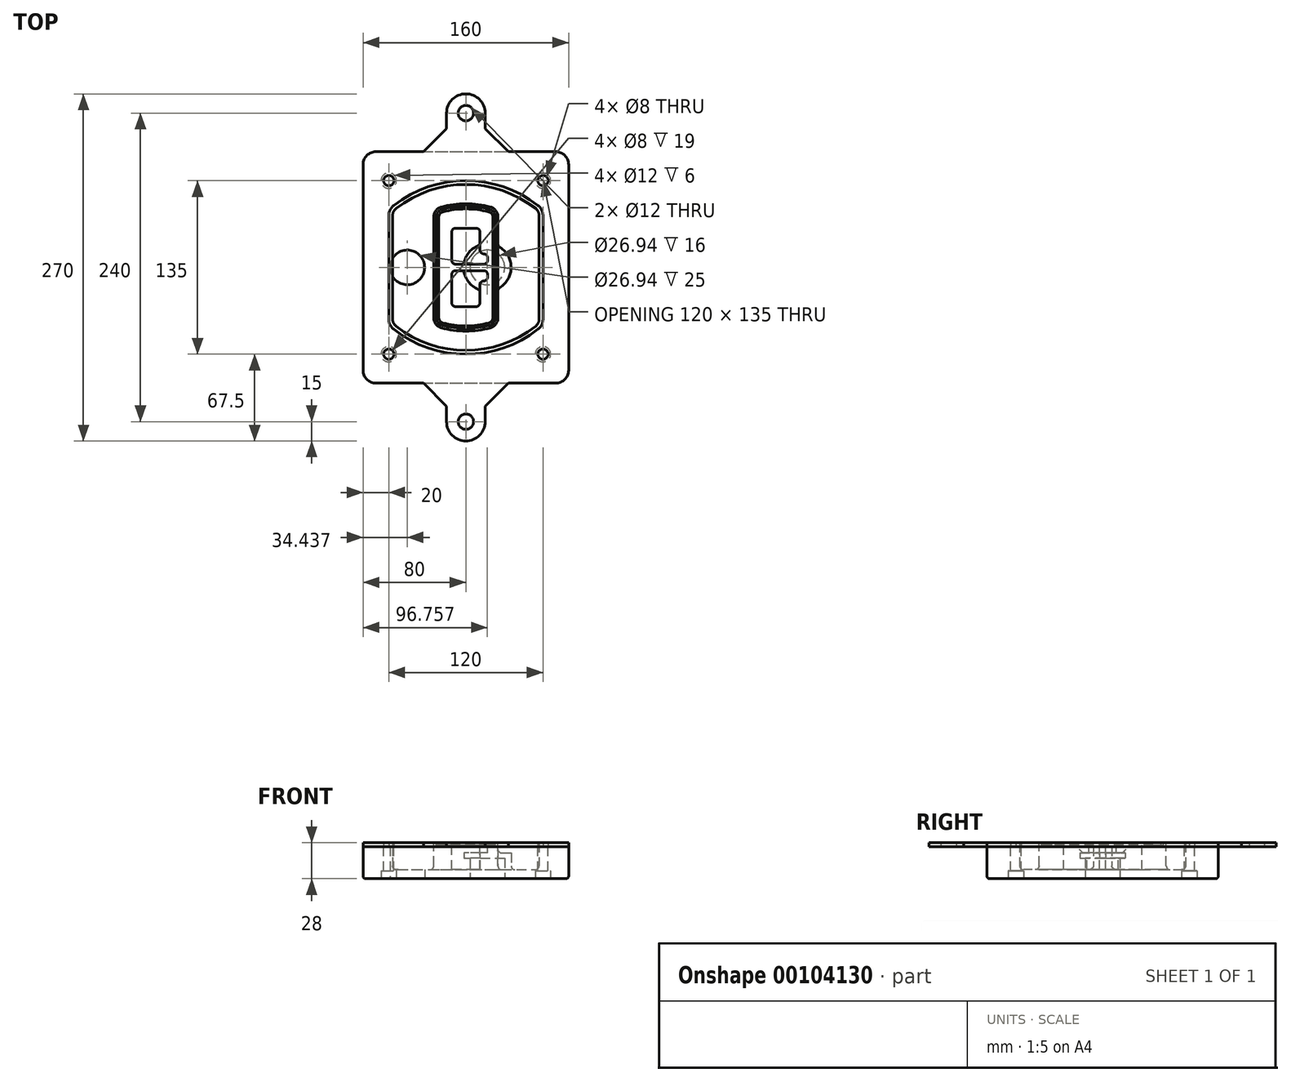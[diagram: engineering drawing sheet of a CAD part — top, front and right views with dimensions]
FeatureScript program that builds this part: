
annotation { "Feature Type Name" : "Feature", "Feature Type Description" : "" }
export const myFeature = defineFeature(function(context is Context, id is Id, definition is map)
    precondition{}
    {
        {
            var Q0;
            Q0=qCreatedBy(makeId("Top.planeOp"),FACE);
            var sketch = newSketch(context, id + "F0", { "sketchPlane" : qUnion([Q0])});
            skPoint(sketch, "E0.rect.middle", {"position": v(0, 0) * mm});
            skLineSegment(sketch, "E1.bottom", {"start": v(-70, -90) * mm, "end": v(70, -90) * mm});
            skLineSegment(sketch, "E1.top", {"start": v(-70, 90) * mm, "end": v(70, 90) * mm});
            skLineSegment(sketch, "E1.left", {"start": v(-80, -80) * mm, "end": v(-80, 80) * mm});
            skLineSegment(sketch, "E1.right", {"start": v(80, -80) * mm, "end": v(80, 80) * mm});
            skLineSegment(sketch, "E2", {"start": v(-80, 90) * mm, "end": v(80, -90) * mm, "construction": true});
            skLineSegment(sketch, "E3", {"start": v(80, 90) * mm, "end": v(-80, -90) * mm, "construction": true});
            skCircle(sketch, "E4", {"center": v(-60, 67.5) * mm, "radius": 4 * mm});
            skCircle(sketch, "E5", {"center": v(60, 67.5) * mm, "radius": 4 * mm});
            skCircle(sketch, "E6", {"center": v(60, -67.5) * mm, "radius": 4 * mm});
            skCircle(sketch, "E7", {"center": v(-60, -67.5) * mm, "radius": 4 * mm});
            skLineSegment(sketch, "E8", {"start": v(-60, 67.5) * mm, "end": v(60, 67.5) * mm, "construction": true});
            skLineSegment(sketch, "E9", {"start": v(60, 67.5) * mm, "end": v(60, -67.5) * mm, "construction": true});
            skLineSegment(sketch, "E10", {"start": v(60, -67.5) * mm, "end": v(-60, -67.5) * mm, "construction": true});
            skLineSegment(sketch, "E11", {"start": v(-60, -67.5) * mm, "end": v(-60, 67.5) * mm, "construction": true});
            skLineSegment(sketch, "E12", {"start": v(-60, 40.3) * mm, "end": v(-60, -40.3) * mm});
            skLineSegment(sketch, "E13", {"start": v(60, 40.3) * mm, "end": v(60, -40.3) * mm});
            skArc(sketch, "E14", {"start": v(56.15, 48.18) * mm, "mid": v(0, 67.5) * mm, "end": v(-56.15, 48.18) * mm});
            skArc(sketch, "E15", {"start": v(-56.15, -48.18) * mm, "mid": v(0, -67.5) * mm, "end": v(56.15, -48.18) * mm});
            skLineSegment(sketch, "E16", {"start": v(-60, 0) * mm, "end": v(60, 0) * mm, "construction": true});
            skPoint(sketch, "E17.visualSharp", {"position": v(-60, -45) * mm});
            skArc(sketch, "E17.filletArc", {"start": v(-60, -40.3) * mm, "mid": v(-58.99, -44.68) * mm, "end": v(-56.15, -48.18) * mm});
            skPoint(sketch, "E18.visualSharp", {"position": v(-60, 45) * mm});
            skArc(sketch, "E18.filletArc", {"start": v(-56.15, 48.18) * mm, "mid": v(-58.99, 44.68) * mm, "end": v(-60, 40.3) * mm});
            skPoint(sketch, "E19.visualSharp", {"position": v(60, 45) * mm});
            skArc(sketch, "E19.filletArc", {"start": v(60, 40.3) * mm, "mid": v(58.99, 44.68) * mm, "end": v(56.15, 48.18) * mm});
            skPoint(sketch, "E20.visualSharp", {"position": v(60, -45) * mm});
            skArc(sketch, "E20.filletArc", {"start": v(56.15, -48.18) * mm, "mid": v(58.99, -44.68) * mm, "end": v(60, -40.3) * mm});
            skPoint(sketch, "E21.visualSharp", {"position": v(-80, 90) * mm});
            skArc(sketch, "E21.filletArc", {"start": v(-70, 90) * mm, "mid": v(-77.07, 87.07) * mm, "end": v(-80, 80) * mm});
            skPoint(sketch, "E22.visualSharp", {"position": v(80, 90) * mm});
            skArc(sketch, "E22.filletArc", {"start": v(80, 80) * mm, "mid": v(77.07, 87.07) * mm, "end": v(70, 90) * mm});
            skPoint(sketch, "E23.visualSharp", {"position": v(80, -90) * mm});
            skArc(sketch, "E23.filletArc", {"start": v(70, -90) * mm, "mid": v(77.07, -87.07) * mm, "end": v(80, -80) * mm});
            skPoint(sketch, "E24.visualSharp", {"position": v(-80, -90) * mm});
            skArc(sketch, "E24.filletArc", {"start": v(-80, -80) * mm, "mid": v(-77.07, -87.07) * mm, "end": v(-70, -90) * mm});
            skArc(sketch, "E25.0", {"start": v(57, 40.3) * mm, "mid": v(56.3, 43.36) * mm, "end": v(54.3, 45.81) * mm});
            skLineSegment(sketch, "E25.1", {"start": v(57, 40.3) * mm, "end": v(57, -40.3) * mm});
            skArc(sketch, "E25.2", {"start": v(54.3, -45.81) * mm, "mid": v(56.3, -43.36) * mm, "end": v(57, -40.3) * mm});
            skArc(sketch, "E25.3", {"start": v(-54.3, -45.81) * mm, "mid": v(0, -64.5) * mm, "end": v(54.3, -45.81) * mm});
            skArc(sketch, "E25.4", {"start": v(-57, -40.3) * mm, "mid": v(-56.3, -43.36) * mm, "end": v(-54.3, -45.81) * mm});
            skArc(sketch, "E25.5", {"start": v(54.3, 45.81) * mm, "mid": v(0, 64.5) * mm, "end": v(-54.3, 45.81) * mm});
            skLineSegment(sketch, "E25.6", {"start": v(-57, 40.3) * mm, "end": v(-57, -40.3) * mm});
            skArc(sketch, "E25.7", {"start": v(-54.3, 45.81) * mm, "mid": v(-56.3, 43.36) * mm, "end": v(-57, 40.3) * mm});
            skArc(sketch, "E26.0", {"start": v(-58.62, 51.33) * mm, "mid": v(-62.58, 46.43) * mm, "end": v(-64, 40.3) * mm});
            skArc(sketch, "E26.1", {"start": v(58.62, 51.33) * mm, "mid": v(0, 71.5) * mm, "end": v(-58.62, 51.33) * mm});
            skArc(sketch, "E26.2", {"start": v(64, 40.3) * mm, "mid": v(62.58, 46.43) * mm, "end": v(58.62, 51.33) * mm});
            skLineSegment(sketch, "E26.3", {"start": v(64, 40.3) * mm, "end": v(64, -40.3) * mm});
            skArc(sketch, "E26.4", {"start": v(58.62, -51.33) * mm, "mid": v(62.58, -46.43) * mm, "end": v(64, -40.3) * mm});
            skLineSegment(sketch, "E26.5", {"start": v(-64, 40.3) * mm, "end": v(-64, -40.3) * mm});
            skArc(sketch, "E26.6", {"start": v(-58.62, -51.33) * mm, "mid": v(0, -71.5) * mm, "end": v(58.62, -51.33) * mm});
            skArc(sketch, "E26.7", {"start": v(-64, -40.3) * mm, "mid": v(-62.58, -46.43) * mm, "end": v(-58.62, -51.33) * mm});
            skSolve(sketch);
        }
        {
            var Q0;
            Q0=makeQuery(id+"F0.imprint","IMPRINT",FACE,{"disambiguationData":[TD([[makeQuery(id+"F0.imprint","IMPRINT",EDGE,{"derivedFrom":sQuery(id+"F0.wireOp",EDGE,"E1.bottom")}),1.0]])]});
            var Q1;
            Q1=makeQuery(id+"F0.imprint","IMPRINT",FACE,{"disambiguationData":[TD([[makeQuery(id+"F0.imprint","IMPRINT",EDGE,{"derivedFrom":sQuery(id+"F0.wireOp",EDGE,"E12")}),1.0]])]});
            var Q2;
            Q2=makeQuery(id+"F0.imprint","IMPRINT",FACE,{"disambiguationData":[TD([[makeQuery(id+"F0.imprint","IMPRINT",EDGE,{"derivedFrom":sQuery(id+"F0.wireOp",EDGE,"E25.0")}),1.0]])]});
            var Q3;
            Q3=makeQuery(id+"F0.imprint","IMPRINT",FACE,{"disambiguationData":[TD([[makeQuery(id+"F0.imprint","IMPRINT",EDGE,{"derivedFrom":sQuery(id+"F0.wireOp",EDGE,"E12")}),-1.0]])]});
            extrude(context, id + "F1", {"entities" : qUnion([Q0, Q1, Q2, Q3]), "oppositeDirection" : true, "depth" : 25 * mm});
        }
        {
            var Q0;
            Q0=makeQuery(id+"F0.imprint","IMPRINT",FACE,{"disambiguationData":[TD([[makeQuery(id+"F0.imprint","IMPRINT",EDGE,{"derivedFrom":sQuery(id+"F0.wireOp",EDGE,"E12")}),1.0]])]});
            extrude(context, id + "F2", {"entities" : qUnion([Q0]), "operationType" : NewBodyOperationType.ADD, "depth" : 3 * mm});
        }
        {
            var Q0;
            Q0=makeQuery(id+"F0.imprint","IMPRINT",FACE,{"disambiguationData":[TD([[makeQuery(id+"F0.imprint","IMPRINT",EDGE,{"derivedFrom":sQuery(id+"F0.wireOp",EDGE,"E25.0")}),1.0]])]});
            extrude(context, id + "F3", {"entities" : qUnion([Q0]), "operationType" : NewBodyOperationType.REMOVE, "oppositeDirection" : true, "depth" : 18 * mm});
        }
        {
            var Q0;
            Q0=makeQuery(id+"F2.opExtrude","CAP_FACE",FACE,{"disambiguationData":[OSD([sQuery(id+"F0.wireOp",EDGE,"E12"),sQuery(id+"F0.wireOp",EDGE,"E13"),sQuery(id+"F0.wireOp",EDGE,"E14"),sQuery(id+"F0.wireOp",EDGE,"E15"),sQuery(id+"F0.wireOp",EDGE,"E17.filletArc"),sQuery(id+"F0.wireOp",EDGE,"E18.filletArc"),sQuery(id+"F0.wireOp",EDGE,"E19.filletArc"),sQuery(id+"F0.wireOp",EDGE,"E20.filletArc"),sQuery(id+"F0.wireOp",EDGE,"E25.0"),sQuery(id+"F0.wireOp",EDGE,"E25.1"),sQuery(id+"F0.wireOp",EDGE,"E25.2"),sQuery(id+"F0.wireOp",EDGE,"E25.3"),sQuery(id+"F0.wireOp",EDGE,"E25.4"),sQuery(id+"F0.wireOp",EDGE,"E25.5"),sQuery(id+"F0.wireOp",EDGE,"E25.6"),sQuery(id+"F0.wireOp",EDGE,"E25.7")])],"isStart":false});
            var sketch = newSketch(context, id + "F4", { "sketchPlane" : qUnion([Q0])});
            skArc(sketch, "E27.0", {"start": v(-19.08, -46.97) * mm, "mid": v(0, -49.5) * mm, "end": v(19.08, -46.97) * mm});
            skArc(sketch, "E28.0", {"start": v(19.08, 46.97) * mm, "mid": v(0, 49.5) * mm, "end": v(-19.08, 46.97) * mm});
            skLineSegment(sketch, "E29", {"start": v(-25, 39.25) * mm, "end": v(-25, -39.25) * mm});
            skLineSegment(sketch, "E30", {"start": v(25, 39.25) * mm, "end": v(25, -39.25) * mm});
            skLineSegment(sketch, "E31", {"start": v(-25, 45.1) * mm, "end": v(25, 45.1) * mm, "construction": true});
            skLineSegment(sketch, "E32", {"start": v(-25, -45.1) * mm, "end": v(25, -45.1) * mm, "construction": true});
            skPoint(sketch, "E33.visualSharp", {"position": v(-25, 45.1) * mm});
            skArc(sketch, "E33.filletArc", {"start": v(-19.08, 46.97) * mm, "mid": v(-23.35, 44.11) * mm, "end": v(-25, 39.25) * mm});
            skPoint(sketch, "E34.visualSharp", {"position": v(25, 45.1) * mm});
            skArc(sketch, "E34.filletArc", {"start": v(25, 39.25) * mm, "mid": v(23.35, 44.11) * mm, "end": v(19.08, 46.97) * mm});
            skPoint(sketch, "E35.visualSharp", {"position": v(25, -45.1) * mm});
            skArc(sketch, "E35.filletArc", {"start": v(19.08, -46.97) * mm, "mid": v(23.35, -44.11) * mm, "end": v(25, -39.25) * mm});
            skPoint(sketch, "E36.visualSharp", {"position": v(-25, -45.1) * mm});
            skArc(sketch, "E36.filletArc", {"start": v(-25, -39.25) * mm, "mid": v(-23.35, -44.11) * mm, "end": v(-19.08, -46.97) * mm});
            skArc(sketch, "E37.0", {"start": v(54.3, 45.81) * mm, "mid": v(0, 64.5) * mm, "end": v(-54.3, 45.81) * mm});
            skArc(sketch, "E37.1", {"start": v(-54.3, 45.81) * mm, "mid": v(-56.3, 43.36) * mm, "end": v(-57, 40.3) * mm});
            skLineSegment(sketch, "E37.2", {"start": v(-57, 40.3) * mm, "end": v(-57, -40.3) * mm});
            skArc(sketch, "E37.3", {"start": v(-57, -40.3) * mm, "mid": v(-56.3, -43.36) * mm, "end": v(-54.3, -45.81) * mm});
            skArc(sketch, "E37.4", {"start": v(-54.3, -45.81) * mm, "mid": v(0, -64.5) * mm, "end": v(54.3, -45.81) * mm});
            skArc(sketch, "E37.5", {"start": v(54.3, -45.81) * mm, "mid": v(56.3, -43.36) * mm, "end": v(57, -40.3) * mm});
            skLineSegment(sketch, "E37.6", {"start": v(57, 40.3) * mm, "end": v(57, -40.3) * mm});
            skArc(sketch, "E37.7", {"start": v(57, 40.3) * mm, "mid": v(56.3, 43.36) * mm, "end": v(54.3, 45.81) * mm});
            skLineSegment(sketch, "E38.0", {"start": v(23, 39.25) * mm, "end": v(23, -39.25) * mm});
            skArc(sketch, "E38.1", {"start": v(18.56, -45.04) * mm, "mid": v(21.76, -42.9) * mm, "end": v(23, -39.25) * mm});
            skArc(sketch, "E38.2", {"start": v(-18.56, -45.04) * mm, "mid": v(0, -47.5) * mm, "end": v(18.56, -45.04) * mm});
            skArc(sketch, "E38.3", {"start": v(-23, -39.25) * mm, "mid": v(-21.76, -42.9) * mm, "end": v(-18.56, -45.04) * mm});
            skLineSegment(sketch, "E38.4", {"start": v(-23, 39.25) * mm, "end": v(-23, -39.25) * mm});
            skArc(sketch, "E38.5", {"start": v(23, 39.25) * mm, "mid": v(21.76, 42.9) * mm, "end": v(18.56, 45.04) * mm});
            skArc(sketch, "E38.6", {"start": v(-18.56, 45.04) * mm, "mid": v(-21.76, 42.9) * mm, "end": v(-23, 39.25) * mm});
            skArc(sketch, "E38.7", {"start": v(18.56, 45.04) * mm, "mid": v(0, 47.5) * mm, "end": v(-18.56, 45.04) * mm});
            skArc(sketch, "E39.0", {"start": v(21, 39.25) * mm, "mid": v(20.18, 41.68) * mm, "end": v(18.04, 43.1) * mm});
            skLineSegment(sketch, "E39.1", {"start": v(21, 39.25) * mm, "end": v(21, -39.25) * mm});
            skArc(sketch, "E39.2", {"start": v(18.04, -43.1) * mm, "mid": v(20.18, -41.68) * mm, "end": v(21, -39.25) * mm});
            skArc(sketch, "E39.3", {"start": v(-18.04, -43.1) * mm, "mid": v(0, -45.5) * mm, "end": v(18.04, -43.1) * mm});
            skArc(sketch, "E39.4", {"start": v(-21, -39.25) * mm, "mid": v(-20.18, -41.68) * mm, "end": v(-18.04, -43.1) * mm});
            skArc(sketch, "E39.5", {"start": v(18.04, 43.1) * mm, "mid": v(0, 45.5) * mm, "end": v(-18.04, 43.1) * mm});
            skLineSegment(sketch, "E39.6", {"start": v(-21, 39.25) * mm, "end": v(-21, -39.25) * mm});
            skArc(sketch, "E39.7", {"start": v(-18.04, 43.1) * mm, "mid": v(-20.18, 41.68) * mm, "end": v(-21, 39.25) * mm});
            skLineSegment(sketch, "E40", {"start": v(-25, 0) * mm, "end": v(25, 0) * mm, "construction": true});
            skLineSegment(sketch, "E41", {"start": v(-11, 5.5) * mm, "end": v(-11, 27.5) * mm});
            skLineSegment(sketch, "E42", {"start": v(-8, 30.5) * mm, "end": v(8, 30.5) * mm});
            skLineSegment(sketch, "E43", {"start": v(11, 27.5) * mm, "end": v(11, 13.5) * mm});
            skLineSegment(sketch, "E44", {"start": v(14, 10.5) * mm, "end": v(14, 10.5) * mm});
            skLineSegment(sketch, "E45", {"start": v(17, 7.5) * mm, "end": v(17, 5.5) * mm});
            skLineSegment(sketch, "E46", {"start": v(14, 2.5) * mm, "end": v(-8, 2.5) * mm});
            skPoint(sketch, "E47.visualSharp", {"position": v(-11, 30.5) * mm});
            skArc(sketch, "E47.filletArc", {"start": v(-8, 30.5) * mm, "mid": v(-10.12, 29.62) * mm, "end": v(-11, 27.5) * mm});
            skPoint(sketch, "E48.visualSharp", {"position": v(11, 30.5) * mm});
            skArc(sketch, "E48.filletArc", {"start": v(11, 27.5) * mm, "mid": v(10.12, 29.62) * mm, "end": v(8, 30.5) * mm});
            skPoint(sketch, "E49.visualSharp", {"position": v(11, 10.5) * mm});
            skArc(sketch, "E49.filletArc", {"start": v(11, 13.5) * mm, "mid": v(11.88, 11.38) * mm, "end": v(14, 10.5) * mm});
            skPoint(sketch, "E50.visualSharp", {"position": v(17, 10.5) * mm});
            skArc(sketch, "E50.filletArc", {"start": v(17, 7.5) * mm, "mid": v(16.12, 9.62) * mm, "end": v(14, 10.5) * mm});
            skPoint(sketch, "E51.visualSharp", {"position": v(17, 2.5) * mm});
            skArc(sketch, "E51.filletArc", {"start": v(14, 2.5) * mm, "mid": v(16.12, 3.38) * mm, "end": v(17, 5.5) * mm});
            skPoint(sketch, "E52.visualSharp", {"position": v(-11, 2.5) * mm});
            skArc(sketch, "E52.filletArc", {"start": v(-11, 5.5) * mm, "mid": v(-10.12, 3.38) * mm, "end": v(-8, 2.5) * mm});
            skLineSegment(sketch, "E53.0.MirrorCS", {"start": v(14, -2.5) * mm, "end": v(-8, -2.5) * mm});
            skArc(sketch, "E54.0.MirrorCS", {"start": v(-11, -5.5) * mm, "mid": v(-10.12, -3.38) * mm, "end": v(-8, -2.5) * mm});
            skLineSegment(sketch, "E55.0.MirrorCS", {"start": v(-11, -5.5) * mm, "end": v(-11, -27.5) * mm});
            skArc(sketch, "E56.0.MirrorCS", {"start": v(-8, -30.5) * mm, "mid": v(-10.12, -29.62) * mm, "end": v(-11, -27.5) * mm});
            skLineSegment(sketch, "E57.0.MirrorCS", {"start": v(-8, -30.5) * mm, "end": v(8, -30.5) * mm});
            skArc(sketch, "E58.0.MirrorCS", {"start": v(11, -27.5) * mm, "mid": v(10.12, -29.62) * mm, "end": v(8, -30.5) * mm});
            skLineSegment(sketch, "E59.0.MirrorCS", {"start": v(11, -27.5) * mm, "end": v(11, -13.5) * mm});
            skArc(sketch, "E60.0.MirrorCS", {"start": v(11, -13.5) * mm, "mid": v(11.88, -11.38) * mm, "end": v(14, -10.5) * mm});
            skArc(sketch, "E61.0.MirrorCS", {"start": v(17, -7.5) * mm, "mid": v(16.12, -9.62) * mm, "end": v(14, -10.5) * mm});
            skLineSegment(sketch, "E62.0.MirrorCS", {"start": v(17, -7.5) * mm, "end": v(17, -5.5) * mm});
            skArc(sketch, "E63.0.MirrorCS", {"start": v(14, -2.5) * mm, "mid": v(16.12, -3.38) * mm, "end": v(17, -5.5) * mm});
            skSolve(sketch);
        }
        {
            var Q0;
            Q0=makeQuery(id+"F4.imprint","IMPRINT",FACE,{"disambiguationData":[TD([[makeQuery(id+"F4.imprint","IMPRINT",EDGE,{"derivedFrom":sQuery(id+"F4.wireOp",EDGE,"E27.0")}),1.0]])]});
            var Q1;
            Q1=makeQuery(id+"F4.imprint","IMPRINT",FACE,{"disambiguationData":[TD([[makeQuery(id+"F4.imprint","IMPRINT",EDGE,{"derivedFrom":sQuery(id+"F4.wireOp",EDGE,"E38.0")}),-1.0]])]});
            var Q2;
            Q2=makeQuery(id+"F4.imprint","IMPRINT",FACE,{"disambiguationData":[TD([[makeQuery(id+"F4.imprint","IMPRINT",EDGE,{"derivedFrom":sQuery(id+"F4.wireOp",EDGE,"E39.0")}),1.0]])]});
            extrude(context, id + "F5", {"entities" : qUnion([Q0, Q1, Q2]), "operationType" : NewBodyOperationType.ADD, "endBound" : BoundingType.UP_TO_NEXT, "oppositeDirection" : true, "depth" : 25 * mm});
        }
        {
            var Q0;
            Q0=makeQuery(id+"F4.imprint","IMPRINT",FACE,{"disambiguationData":[TD([[makeQuery(id+"F4.imprint","IMPRINT",EDGE,{"derivedFrom":sQuery(id+"F4.wireOp",EDGE,"E38.0")}),-1.0]])]});
            extrude(context, id + "F6", {"entities" : qUnion([Q0]), "operationType" : NewBodyOperationType.REMOVE, "oppositeDirection" : true, "depth" : 2 * mm});
        }
        {
            var Q0;
            Q0=makeQuery(id+"F1.opExtrude","CAP_FACE",FACE,{"disambiguationData":[OSD([sQuery(id+"F0.wireOp",EDGE,"E1.bottom"),sQuery(id+"F0.wireOp",EDGE,"E1.top"),sQuery(id+"F0.wireOp",EDGE,"E1.left"),sQuery(id+"F0.wireOp",EDGE,"E1.right"),sQuery(id+"F0.wireOp",EDGE,"E4"),sQuery(id+"F0.wireOp",EDGE,"E5"),sQuery(id+"F0.wireOp",EDGE,"E6"),sQuery(id+"F0.wireOp",EDGE,"E7"),sQuery(id+"F0.wireOp",EDGE,"E21.filletArc"),sQuery(id+"F0.wireOp",EDGE,"E22.filletArc"),sQuery(id+"F0.wireOp",EDGE,"E23.filletArc"),sQuery(id+"F0.wireOp",EDGE,"E24.filletArc")])],"isStart":false});
            var sketch = newSketch(context, id + "F7", { "sketchPlane" : qUnion([Q0])});
            skCircle(sketch, "E64", {"center": v(16.76, 0) * mm, "radius": 13.47 * mm});
            skCircle(sketch, "E65", {"center": v(-45.56, 0) * mm, "radius": 13.47 * mm});
            skLineSegment(sketch, "E66", {"start": v(80, 0) * mm, "end": v(-80, 0) * mm});
            skCircle(sketch, "E67", {"center": v(16.76, 0) * mm, "radius": 18.47 * mm});
            skCircle(sketch, "E68", {"center": v(60, -67.5) * mm, "radius": 6 * mm});
            skCircle(sketch, "E69", {"center": v(-60, -67.5) * mm, "radius": 6 * mm});
            skCircle(sketch, "E70", {"center": v(-60, 67.5) * mm, "radius": 6 * mm});
            skCircle(sketch, "E71", {"center": v(60, 67.5) * mm, "radius": 6 * mm});
            skSolve(sketch);
        }
        {
            var Q0;
            {var subQ1=sQuery(id+"F7.wireOp",EDGE,"E66");var subQ4=sQuery(id+"F7.wireOp",EDGE,"E64");var subQ6=makeQuery(id+"F7.imprint","INTERSECT",VERTEX,{"disambiguationData":[OD(0.0)],"derivedFrom":[subQ4,subQ1]});Q0=makeQuery(id+"F7.imprint","IMPRINT",FACE,{"disambiguationData":[TD([[makeQuery(id+"F7.imprint","IMPRINT",EDGE,{"disambiguationData":[TD([[subQ6,-1.0]])],"derivedFrom":subQ4}),-1.0]])]});}
            var Q1;
            {var subQ0=sQuery(id+"F7.wireOp",EDGE,"E66");var subQ1=sQuery(id+"F7.wireOp",EDGE,"E64");var subQ3=makeQuery(id+"F7.imprint","INTERSECT",VERTEX,{"disambiguationData":[OD(0.0)],"derivedFrom":[subQ1,subQ0]});Q1=makeQuery(id+"F7.imprint","IMPRINT",FACE,{"disambiguationData":[TD([[makeQuery(id+"F7.imprint","IMPRINT",EDGE,{"disambiguationData":[TD([[subQ3,-1.0]])],"derivedFrom":subQ1}),1.0]])]});}
            var Q2;
            {var subQ0=sQuery(id+"F7.wireOp",EDGE,"E66");var subQ1=sQuery(id+"F7.wireOp",EDGE,"E64");var subQ3=makeQuery(id+"F7.imprint","INTERSECT",VERTEX,{"disambiguationData":[OD(0.0)],"derivedFrom":[subQ1,subQ0]});Q2=makeQuery(id+"F7.imprint","IMPRINT",FACE,{"disambiguationData":[TD([[makeQuery(id+"F7.imprint","IMPRINT",EDGE,{"disambiguationData":[TD([[subQ3,1.0]])],"derivedFrom":subQ1}),1.0]])]});}
            var Q3;
            {var subQ1=sQuery(id+"F7.wireOp",EDGE,"E66");var subQ4=sQuery(id+"F7.wireOp",EDGE,"E64");var subQ6=makeQuery(id+"F7.imprint","INTERSECT",VERTEX,{"disambiguationData":[OD(0.0)],"derivedFrom":[subQ4,subQ1]});Q3=makeQuery(id+"F7.imprint","IMPRINT",FACE,{"disambiguationData":[TD([[makeQuery(id+"F7.imprint","IMPRINT",EDGE,{"disambiguationData":[TD([[subQ6,1.0]])],"derivedFrom":subQ4}),-1.0]])]});}
            extrude(context, id + "F8", {"entities" : qUnion([Q0, Q1, Q2, Q3]), "operationType" : NewBodyOperationType.ADD, "oppositeDirection" : true, "depth" : 20 * mm});
        }
        {
            var Q0;
            {var subQ0=sQuery(id+"F7.wireOp",EDGE,"E66");var subQ1=sQuery(id+"F7.wireOp",EDGE,"E64");var subQ3=makeQuery(id+"F7.imprint","INTERSECT",VERTEX,{"disambiguationData":[OD(0.0)],"derivedFrom":[subQ1,subQ0]});Q0=makeQuery(id+"F7.imprint","IMPRINT",FACE,{"disambiguationData":[TD([[makeQuery(id+"F7.imprint","IMPRINT",EDGE,{"disambiguationData":[TD([[subQ3,-1.0]])],"derivedFrom":subQ1}),1.0]])]});}
            var Q1;
            {var subQ0=sQuery(id+"F7.wireOp",EDGE,"E66");var subQ1=sQuery(id+"F7.wireOp",EDGE,"E64");var subQ3=makeQuery(id+"F7.imprint","INTERSECT",VERTEX,{"disambiguationData":[OD(0.0)],"derivedFrom":[subQ1,subQ0]});Q1=makeQuery(id+"F7.imprint","IMPRINT",FACE,{"disambiguationData":[TD([[makeQuery(id+"F7.imprint","IMPRINT",EDGE,{"disambiguationData":[TD([[subQ3,1.0]])],"derivedFrom":subQ1}),1.0]])]});}
            extrude(context, id + "F9", {"entities" : qUnion([Q0, Q1]), "operationType" : NewBodyOperationType.REMOVE, "oppositeDirection" : true, "depth" : 16 * mm});
        }
        {
            var Q0;
            {var subQ0=sQuery(id+"F7.wireOp",EDGE,"E66");var subQ1=sQuery(id+"F7.wireOp",EDGE,"E65");var subQ3=makeQuery(id+"F7.imprint","INTERSECT",VERTEX,{"disambiguationData":[OD(0.0)],"derivedFrom":[subQ1,subQ0]});Q0=makeQuery(id+"F7.imprint","IMPRINT",FACE,{"disambiguationData":[TD([[makeQuery(id+"F7.imprint","IMPRINT",EDGE,{"disambiguationData":[TD([[subQ3,-1.0]])],"derivedFrom":subQ1}),1.0]])]});}
            var Q1;
            {var subQ0=sQuery(id+"F7.wireOp",EDGE,"E66");var subQ1=sQuery(id+"F7.wireOp",EDGE,"E65");var subQ3=makeQuery(id+"F7.imprint","INTERSECT",VERTEX,{"disambiguationData":[OD(0.0)],"derivedFrom":[subQ1,subQ0]});Q1=makeQuery(id+"F7.imprint","IMPRINT",FACE,{"disambiguationData":[TD([[makeQuery(id+"F7.imprint","IMPRINT",EDGE,{"disambiguationData":[TD([[subQ3,1.0]])],"derivedFrom":subQ1}),1.0]])]});}
            extrude(context, id + "F10", {"entities" : qUnion([Q0, Q1]), "operationType" : NewBodyOperationType.REMOVE, "oppositeDirection" : true, "depth" : 25 * mm});
        }
        {
            var Q0;
            Q0=makeQuery(id+"F7.imprint","IMPRINT",FACE,{"disambiguationData":[TD([[makeQuery(id+"F7.imprint","IMPRINT",EDGE,{"derivedFrom":sQuery(id+"F7.wireOp",EDGE,"E68")}),1.0]])]});
            var Q1;
            Q1=makeQuery(id+"F7.imprint","IMPRINT",FACE,{"disambiguationData":[TD([[makeQuery(id+"F7.imprint","IMPRINT",EDGE,{"derivedFrom":makeQuery(id+"F1.opExtrude","CAP_EDGE",EDGE,{"disambiguationData":[OSD([sQuery(id+"F0.wireOp",EDGE,"E5")])],"isStart":false})}),-1.0]])]});
            var Q2;
            Q2=makeQuery(id+"F7.imprint","IMPRINT",FACE,{"disambiguationData":[TD([[makeQuery(id+"F7.imprint","IMPRINT",EDGE,{"derivedFrom":sQuery(id+"F7.wireOp",EDGE,"E69")}),1.0]])]});
            var Q3;
            Q3=makeQuery(id+"F7.imprint","IMPRINT",FACE,{"disambiguationData":[TD([[makeQuery(id+"F7.imprint","IMPRINT",EDGE,{"derivedFrom":makeQuery(id+"F1.opExtrude","CAP_EDGE",EDGE,{"disambiguationData":[OSD([sQuery(id+"F0.wireOp",EDGE,"E4")])],"isStart":false})}),-1.0]])]});
            var Q4;
            Q4=makeQuery(id+"F7.imprint","IMPRINT",FACE,{"disambiguationData":[TD([[makeQuery(id+"F7.imprint","IMPRINT",EDGE,{"derivedFrom":sQuery(id+"F7.wireOp",EDGE,"E70")}),1.0]])]});
            var Q5;
            Q5=makeQuery(id+"F7.imprint","IMPRINT",FACE,{"disambiguationData":[TD([[makeQuery(id+"F7.imprint","IMPRINT",EDGE,{"derivedFrom":makeQuery(id+"F1.opExtrude","CAP_EDGE",EDGE,{"disambiguationData":[OSD([sQuery(id+"F0.wireOp",EDGE,"E7")])],"isStart":false})}),-1.0]])]});
            var Q6;
            Q6=makeQuery(id+"F7.imprint","IMPRINT",FACE,{"disambiguationData":[TD([[makeQuery(id+"F7.imprint","IMPRINT",EDGE,{"derivedFrom":sQuery(id+"F7.wireOp",EDGE,"E71")}),1.0]])]});
            var Q7;
            Q7=makeQuery(id+"F7.imprint","IMPRINT",FACE,{"disambiguationData":[TD([[makeQuery(id+"F7.imprint","IMPRINT",EDGE,{"derivedFrom":makeQuery(id+"F1.opExtrude","CAP_EDGE",EDGE,{"disambiguationData":[OSD([sQuery(id+"F0.wireOp",EDGE,"E6")])],"isStart":false})}),-1.0]])]});
            extrude(context, id + "F11", {"entities" : qUnion([Q0, Q1, Q2, Q3, Q4, Q5, Q6, Q7]), "operationType" : NewBodyOperationType.REMOVE, "oppositeDirection" : true, "depth" : 6 * mm});
        }
        {
            var Q0;
            Q0=makeQuery(id+"F9.boolean.opBoolean","COPY",FACE,{"derivedFrom":makeQuery(id+"F9.opExtrude","CAP_FACE",FACE,{"disambiguationData":[OSD([sQuery(id+"F7.wireOp",EDGE,"E64")])],"isStart":false})});
            var sketch = newSketch(context, id + "F12", { "sketchPlane" : qUnion([Q0])});
            skArc(sketch, "E72.0", {"start": v(11, 17.55) * mm, "mid": v(2.57, 11.82) * mm, "end": v(-1.54, 2.5) * mm});
            skArc(sketch, "E72.1", {"start": v(-1.54, -2.5) * mm, "mid": v(2.57, -11.82) * mm, "end": v(11, -17.55) * mm});
            skLineSegment(sketch, "E73", {"start": v(-1.54, -2.5) * mm, "end": v(14, -2.5) * mm});
            skLineSegment(sketch, "E74.0", {"start": v(14, 2.5) * mm, "end": v(-1.54, 2.5) * mm});
            skArc(sketch, "E74.1", {"start": v(14, 2.5) * mm, "mid": v(16.12, 3.38) * mm, "end": v(17, 5.5) * mm});
            skLineSegment(sketch, "E74.2", {"start": v(17, 7.5) * mm, "end": v(17, 5.5) * mm});
            skArc(sketch, "E74.3", {"start": v(17, 7.5) * mm, "mid": v(16.12, 9.62) * mm, "end": v(14, 10.5) * mm});
            skArc(sketch, "E74.4", {"start": v(11, 13.5) * mm, "mid": v(11.88, 11.38) * mm, "end": v(14, 10.5) * mm});
            skLineSegment(sketch, "E74.5", {"start": v(11, 17.55) * mm, "end": v(11, 13.5) * mm});
            skLineSegment(sketch, "E74.7", {"start": v(14, -2.5) * mm, "end": v(-1.54, -2.5) * mm});
            skArc(sketch, "E74.8", {"start": v(14, -2.5) * mm, "mid": v(16.12, -3.38) * mm, "end": v(17, -5.5) * mm});
            skLineSegment(sketch, "E74.9", {"start": v(17, -7.5) * mm, "end": v(17, -5.5) * mm});
            skArc(sketch, "E74.10", {"start": v(17, -7.5) * mm, "mid": v(16.12, -9.62) * mm, "end": v(14, -10.5) * mm});
            skArc(sketch, "E74.11", {"start": v(11, -13.5) * mm, "mid": v(11.88, -11.38) * mm, "end": v(14, -10.5) * mm});
            skLineSegment(sketch, "E74.12", {"start": v(11, -17.55) * mm, "end": v(11, -13.5) * mm});
            skPoint(sketch, "E75.orphan", {"position": v(11, -27.5) * mm});
            skPoint(sketch, "E76.orphan", {"position": v(-8, -2.5) * mm});
            skPoint(sketch, "E77.orphan", {"position": v(-8, 2.5) * mm});
            skPoint(sketch, "E78.orphan", {"position": v(11, 27.5) * mm});
            skSolve(sketch);
        }
        {
            var Q0;
            {var subQ7=sQuery(id+"F12.wireOp",EDGE,"E72.0");var subQ14=sQuery(id+"F12.wireOp",EDGE,"E72.1");var subQ16=sQuery(id+"F12.wireOp",EDGE,"E74.1");var subQ18=sQuery(id+"F12.wireOp",EDGE,"E74.8");Q0=qUnion([makeQuery(id+"F12.imprint","IMPRINT",FACE,{"disambiguationData":[TD([[makeQuery(id+"F12.imprint","IMPRINT",EDGE,{"derivedFrom":subQ7}),1.0]])]}),makeQuery(id+"F12.imprint","IMPRINT",FACE,{"disambiguationData":[TD([[makeQuery(id+"F12.imprint","IMPRINT",EDGE,{"derivedFrom":subQ14}),1.0]])]}),makeQuery(id+"F12.imprint","IMPRINT",FACE,{"disambiguationData":[TD([[makeQuery(id+"F12.imprint","IMPRINT",EDGE,{"derivedFrom":subQ16}),1.0]])]}),makeQuery(id+"F12.imprint","IMPRINT",FACE,{"disambiguationData":[TD([[makeQuery(id+"F12.imprint","IMPRINT",EDGE,{"derivedFrom":subQ18}),-1.0]])]})]);}
            var Q1;
            Q1=makeQuery(id+"F5.boolean.opBoolean","SPLIT",FACE,{"disambiguationData":[TD([makeQuery(id+"F5.opExtrude","SWEPT_FACE",FACE,{"disambiguationData":[OSD([sQuery(id+"F4.wireOp",EDGE,"E41")])]})])],"derivedFrom":makeQuery(id+"F3.boolean.opBoolean","COPY",FACE,{"derivedFrom":makeQuery(id+"F3.opExtrude","CAP_FACE",FACE,{"disambiguationData":[OSD([sQuery(id+"F0.wireOp",EDGE,"E25.0"),sQuery(id+"F0.wireOp",EDGE,"E25.1"),sQuery(id+"F0.wireOp",EDGE,"E25.2"),sQuery(id+"F0.wireOp",EDGE,"E25.3"),sQuery(id+"F0.wireOp",EDGE,"E25.4"),sQuery(id+"F0.wireOp",EDGE,"E25.5"),sQuery(id+"F0.wireOp",EDGE,"E25.6"),sQuery(id+"F0.wireOp",EDGE,"E25.7")])],"isStart":false})})});
            extrude(context, id + "F13", {"entities" : qUnion([Q0]), "operationType" : NewBodyOperationType.REMOVE, "endBound" : BoundingType.UP_TO_SURFACE, "endBoundEntityFace" : qUnion([Q1]), "depth" : 25 * mm});
        }
        {
            var Q0;
            Q0=makeQuery(id+"F3.boolean.opBoolean","COPY",EDGE,{"derivedFrom":makeQuery(id+"F3.opExtrude","CAP_EDGE",EDGE,{"disambiguationData":[OSD([sQuery(id+"F0.wireOp",EDGE,"E25.6")])],"isStart":false})});
            var Q1;
            Q1=makeQuery(id+"F8.boolean.opBoolean","INTERSECT",EDGE,{"derivedFrom":[makeQuery(id+"F5.opExtrude","SWEPT_FACE",FACE,{"disambiguationData":[OSD([sQuery(id+"F4.wireOp",EDGE,"E30")])]}),makeQuery(id+"F8.opExtrude","CAP_FACE",FACE,{"disambiguationData":[OSD([sQuery(id+"F7.wireOp",EDGE,"E67")])],"isStart":false})]});
            var Q2;
            Q2=makeQuery(id+"F8.boolean.opBoolean","INTERSECT",EDGE,{"disambiguationData":[OD(1.0)],"derivedFrom":[makeQuery(id+"F5.opExtrude","SWEPT_FACE",FACE,{"disambiguationData":[OSD([sQuery(id+"F4.wireOp",EDGE,"E30")])]}),makeQuery(id+"F8.opExtrude","SWEPT_FACE",FACE,{"disambiguationData":[OSD([sQuery(id+"F7.wireOp",EDGE,"E67")])]})]});
            var Q3;
            {var subQ0=sQuery(id+"F4.wireOp",EDGE,"E30");Q3=makeQuery(id+"F8.boolean.opBoolean","SPLIT",EDGE,{"disambiguationData":[TD([makeQuery(id+"F5.opExtrude","SWEPT_FACE",FACE,{"disambiguationData":[OSD([sQuery(id+"F4.wireOp",EDGE,"E35.filletArc")])]})])],"derivedFrom":makeQuery(id+"F5.opExtrude","CAP_EDGE",EDGE,{"disambiguationData":[OSD([subQ0])],"isStart":false})});}
            var Q4;
            {var subQ0=sQuery(id+"F0.wireOp",EDGE,"E25.7");var subQ1=sQuery(id+"F0.wireOp",EDGE,"E25.1");var subQ2=sQuery(id+"F0.wireOp",EDGE,"E25.6");var subQ3=sQuery(id+"F0.wireOp",EDGE,"E25.5");var subQ4=sQuery(id+"F0.wireOp",EDGE,"E25.4");var subQ5=sQuery(id+"F0.wireOp",EDGE,"E25.0");var subQ6=sQuery(id+"F0.wireOp",EDGE,"E25.2");var subQ7=sQuery(id+"F0.wireOp",EDGE,"E25.3");Q4=makeQuery(id+"F8.boolean.opBoolean","INTERSECT",EDGE,{"derivedFrom":[makeQuery(id+"F5.boolean.opBoolean","SPLIT",FACE,{"disambiguationData":[TD([makeQuery(id+"F2.opExtrude","SWEPT_FACE",FACE,{"disambiguationData":[OSD([subQ5])]})])],"derivedFrom":makeQuery(id+"F3.boolean.opBoolean","COPY",FACE,{"derivedFrom":makeQuery(id+"F3.opExtrude","CAP_FACE",FACE,{"disambiguationData":[OSD([subQ5,subQ1,subQ6,subQ7,subQ4,subQ3,subQ2,subQ0])],"isStart":false})})}),makeQuery(id+"F8.opExtrude","SWEPT_FACE",FACE,{"disambiguationData":[OSD([sQuery(id+"F7.wireOp",EDGE,"E67")])]})]});}
            var Q5;
            Q5=makeQuery(id+"F8.boolean.opBoolean","INTERSECT",EDGE,{"disambiguationData":[OD(0.0)],"derivedFrom":[makeQuery(id+"F5.opExtrude","SWEPT_FACE",FACE,{"disambiguationData":[OSD([sQuery(id+"F4.wireOp",EDGE,"E30")])]}),makeQuery(id+"F8.opExtrude","SWEPT_FACE",FACE,{"disambiguationData":[OSD([sQuery(id+"F7.wireOp",EDGE,"E67")])]})]});
            fillet(context, id + "F14", {"entities" : qUnion([Q0, Q1, Q2, Q3, Q4, Q5]), "radius" : 3 * mm, "tangentPropagation" : true, "allowEdgeOverflow" : false});
        }
        {
            var Q0;
            Q0=makeQuery(id+"F1.opExtrude","CAP_EDGE",EDGE,{"disambiguationData":[OSD([sQuery(id+"F0.wireOp",EDGE,"E1.bottom")])],"isStart":false});
            fillet(context, id + "F15", {"entities" : qUnion([Q0]), "radius" : 2 * mm, "tangentPropagation" : true, "allowEdgeOverflow" : false});
        }
        {
            var Q0;
            {var subQ0=sQuery(id+"F0.wireOp",EDGE,"E22.filletArc");var subQ1=sQuery(id+"F0.wireOp",EDGE,"E7");var subQ2=sQuery(id+"F0.wireOp",EDGE,"E6");var subQ3=sQuery(id+"F0.wireOp",EDGE,"E5");var subQ4=sQuery(id+"F0.wireOp",EDGE,"E4");var subQ5=sQuery(id+"F0.wireOp",EDGE,"E1.bottom");var subQ6=sQuery(id+"F0.wireOp",EDGE,"E21.filletArc");var subQ7=sQuery(id+"F0.wireOp",EDGE,"E1.top");var subQ8=sQuery(id+"F0.wireOp",EDGE,"E1.left");var subQ9=sQuery(id+"F0.wireOp",EDGE,"E1.right");var subQ10=sQuery(id+"F0.wireOp",EDGE,"E23.filletArc");var subQ11=sQuery(id+"F0.wireOp",EDGE,"E24.filletArc");Q0=makeQuery(id+"F2.boolean.opBoolean","SPLIT",FACE,{"disambiguationData":[TD([makeQuery(id+"F1.opExtrude","SWEPT_FACE",FACE,{"disambiguationData":[OSD([subQ5])]})])],"derivedFrom":makeQuery(id+"F1.opExtrude","CAP_FACE",FACE,{"disambiguationData":[OSD([subQ5,subQ7,subQ8,subQ9,subQ4,subQ3,subQ2,subQ1,subQ6,subQ0,subQ10,subQ11])],"isStart":true})});}
            var sketch = newSketch(context, id + "F16", { "sketchPlane" : qUnion([Q0])});
            skLineSegment(sketch, "E79", {"start": v(0, 90) * mm, "end": v(0, 120) * mm, "construction": true});
            skLineSegment(sketch, "E80", {"start": v(-33, 90) * mm, "end": v(-15, 108) * mm});
            skLineSegment(sketch, "E81", {"start": v(-15, 108) * mm, "end": v(-15, 120) * mm});
            skLineSegment(sketch, "E82", {"start": v(33, 90) * mm, "end": v(15, 108) * mm});
            skLineSegment(sketch, "E83", {"start": v(15, 108) * mm, "end": v(15, 120) * mm});
            skArc(sketch, "E84", {"start": v(15, 120) * mm, "mid": v(0, 135) * mm, "end": v(-15, 120) * mm});
            skCircle(sketch, "E85", {"center": v(0, 120) * mm, "radius": 6 * mm});
            skLineSegment(sketch, "E86", {"start": v(-80, 0) * mm, "end": v(80, 0) * mm, "construction": true});
            skLineSegment(sketch, "E87.MirrorCS", {"start": v(-33, -90) * mm, "end": v(-15, -108) * mm});
            skLineSegment(sketch, "E88.MirrorCS", {"start": v(33, -90) * mm, "end": v(15, -108) * mm});
            skArc(sketch, "E89.MirrorCS", {"start": v(15, -120) * mm, "mid": v(0, -135) * mm, "end": v(-15, -120) * mm});
            skLineSegment(sketch, "E90.MirrorCS", {"start": v(15, -108) * mm, "end": v(15, -120) * mm});
            skLineSegment(sketch, "E91.MirrorCS", {"start": v(-15, -108) * mm, "end": v(-15, -120) * mm});
            skLineSegment(sketch, "E92.MirrorCS", {"start": v(0, -90) * mm, "end": v(0, -120) * mm, "construction": true});
            skCircle(sketch, "E93.MirrorC", {"center": v(0, -120) * mm, "radius": 6 * mm});
            skSolve(sketch);
        }
        {
            var Q0;
            {var subQ1=sQuery(id+"F16.wireOp",EDGE,"E80");Q0=makeQuery(id+"F16.imprint","IMPRINT",FACE,{"disambiguationData":[TD([[makeQuery(id+"F16.imprint","IMPRINT",EDGE,{"derivedFrom":subQ1}),-1.0]])]});}
            var Q1;
            Q1=makeQuery(id+"F16.imprint","IMPRINT",FACE,{"disambiguationData":[TD([[makeQuery(id+"F16.imprint","IMPRINT",EDGE,{"derivedFrom":makeQuery(id+"F1.opExtrude","CAP_EDGE",EDGE,{"disambiguationData":[OSD([sQuery(id+"F0.wireOp",EDGE,"E1.left")])],"isStart":true})}),-1.0]])]});
            var Q2;
            {var subQ0=sQuery(id+"F16.wireOp",EDGE,"E87.MirrorCS");Q2=makeQuery(id+"F16.imprint","IMPRINT",FACE,{"disambiguationData":[TD([[makeQuery(id+"F16.imprint","IMPRINT",EDGE,{"derivedFrom":subQ0}),1.0]])]});}
            var Q3;
            Q3=makeQuery(id+"F2.opExtrude","CAP_FACE",FACE,{"disambiguationData":[OSD([sQuery(id+"F0.wireOp",EDGE,"E12"),sQuery(id+"F0.wireOp",EDGE,"E13"),sQuery(id+"F0.wireOp",EDGE,"E14"),sQuery(id+"F0.wireOp",EDGE,"E15"),sQuery(id+"F0.wireOp",EDGE,"E17.filletArc"),sQuery(id+"F0.wireOp",EDGE,"E18.filletArc"),sQuery(id+"F0.wireOp",EDGE,"E19.filletArc"),sQuery(id+"F0.wireOp",EDGE,"E20.filletArc"),sQuery(id+"F0.wireOp",EDGE,"E25.0"),sQuery(id+"F0.wireOp",EDGE,"E25.1"),sQuery(id+"F0.wireOp",EDGE,"E25.2"),sQuery(id+"F0.wireOp",EDGE,"E25.3"),sQuery(id+"F0.wireOp",EDGE,"E25.4"),sQuery(id+"F0.wireOp",EDGE,"E25.5"),sQuery(id+"F0.wireOp",EDGE,"E25.6"),sQuery(id+"F0.wireOp",EDGE,"E25.7")])],"isStart":false});
            extrude(context, id + "F17", {"entities" : qUnion([Q0, Q1, Q2]), "endBound" : BoundingType.UP_TO_SURFACE, "endBoundEntityFace" : qUnion([Q3]), "depth" : 25 * mm});
        }
    });
